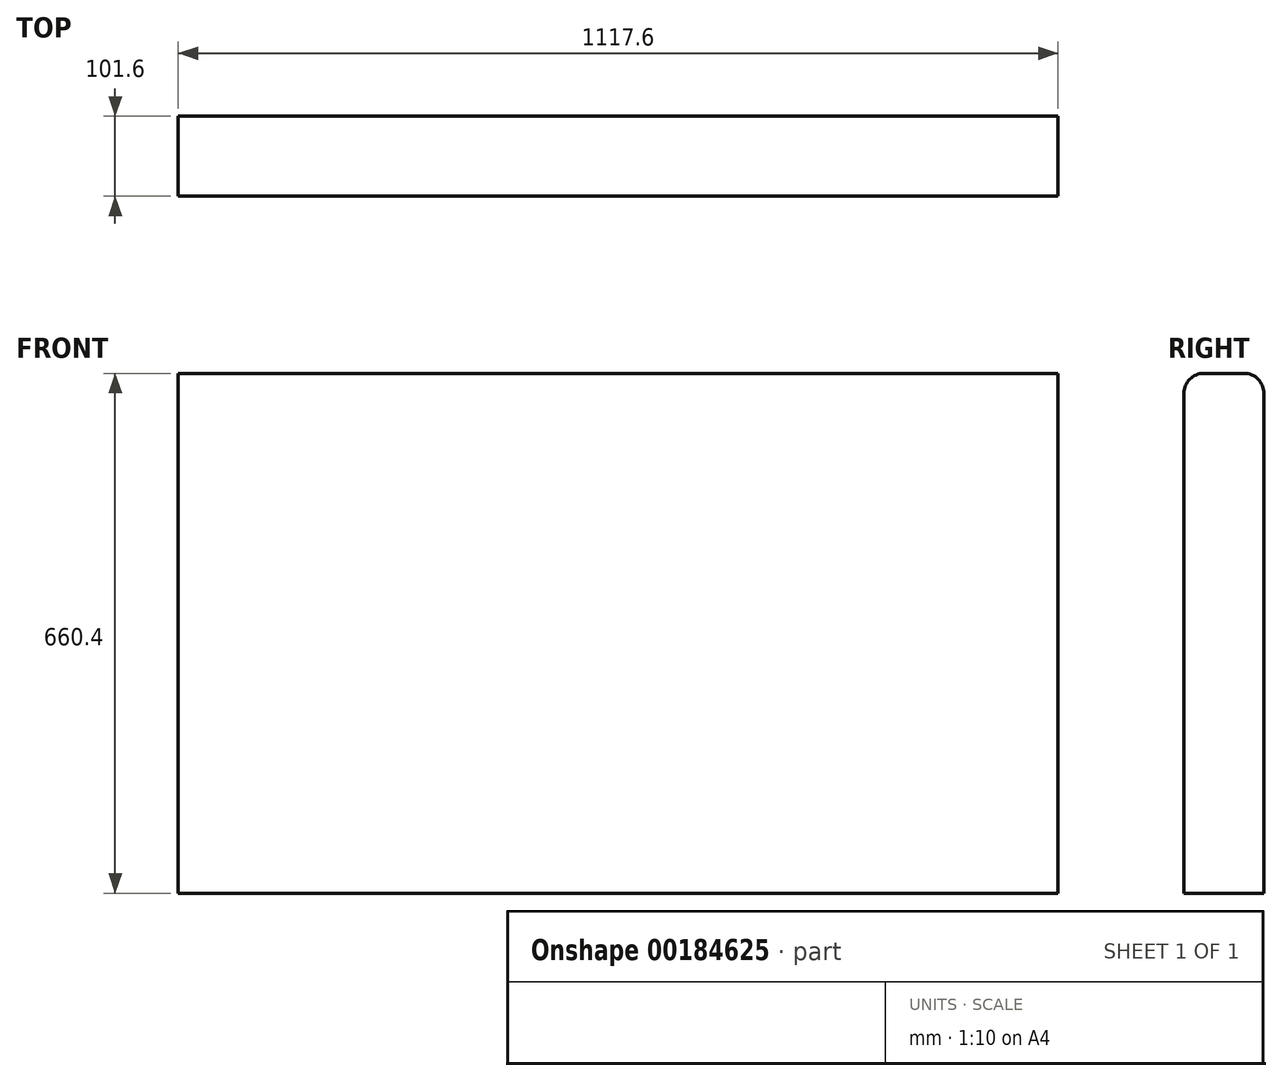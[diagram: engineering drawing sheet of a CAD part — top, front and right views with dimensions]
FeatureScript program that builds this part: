
annotation { "Feature Type Name" : "Feature", "Feature Type Description" : "" }
export const myFeature = defineFeature(function(context is Context, id is Id, definition is map)
    precondition{}
    {
        {
            var Q0;
            Q0=qCreatedBy(makeId("Front.planeOp"),FACE);
            var sketch = newSketch(context, id + "F0", { "sketchPlane" : qUnion([Q0])});
            skLineSegment(sketch, "E0.bottom", {"start": v(558.8, -330.2) * mm, "end": v(-558.8, -330.2) * mm});
            skLineSegment(sketch, "E0.top", {"start": v(558.8, 330.2) * mm, "end": v(-558.8, 330.2) * mm});
            skLineSegment(sketch, "E0.left", {"start": v(558.8, -330.2) * mm, "end": v(558.8, 330.2) * mm});
            skLineSegment(sketch, "E0.right", {"start": v(-558.8, -330.2) * mm, "end": v(-558.8, 330.2) * mm});
            skPoint(sketch, "E0.middle", {"position": v(0, 0) * mm});
            skSolve(sketch);
        }
        {
            var Q0;
            Q0 = qSketchRegion(id + "F0", true);
            var Q1;
            Q1=makeQuery(id+"F0.imprint","IMPRINT",FACE,{"disambiguationData":[TD([[makeQuery(id+"F0.imprint","IMPRINT",EDGE,{"derivedFrom":sQuery(id+"F0.wireOp",EDGE,"E0.bottom")}),-1.0]])]});
            extrude(context, id + "F1", {"entities" : qUnion([Q0, Q1]), "endBound" : BoundingType.SYMMETRIC, "depth" : 101.6 * mm});
        }
        {
            var Q0;
            Q0=makeQuery(id+"F1.opExtrude","CAP_EDGE",EDGE,{"disambiguationData":[OSD([sQuery(id+"F0.wireOp",EDGE,"E0.top")])],"isStart":false});
            var Q1;
            Q1=makeQuery(id+"F1.opExtrude","CAP_EDGE",EDGE,{"disambiguationData":[OSD([sQuery(id+"F0.wireOp",EDGE,"E0.top")])],"isStart":true});
            fillet(context, id + "F2", {"entities" : qUnion([Q0, Q1]), "radius" : 25.4 * mm, "tangentPropagation" : true, "allowEdgeOverflow" : false});
        }
    });
